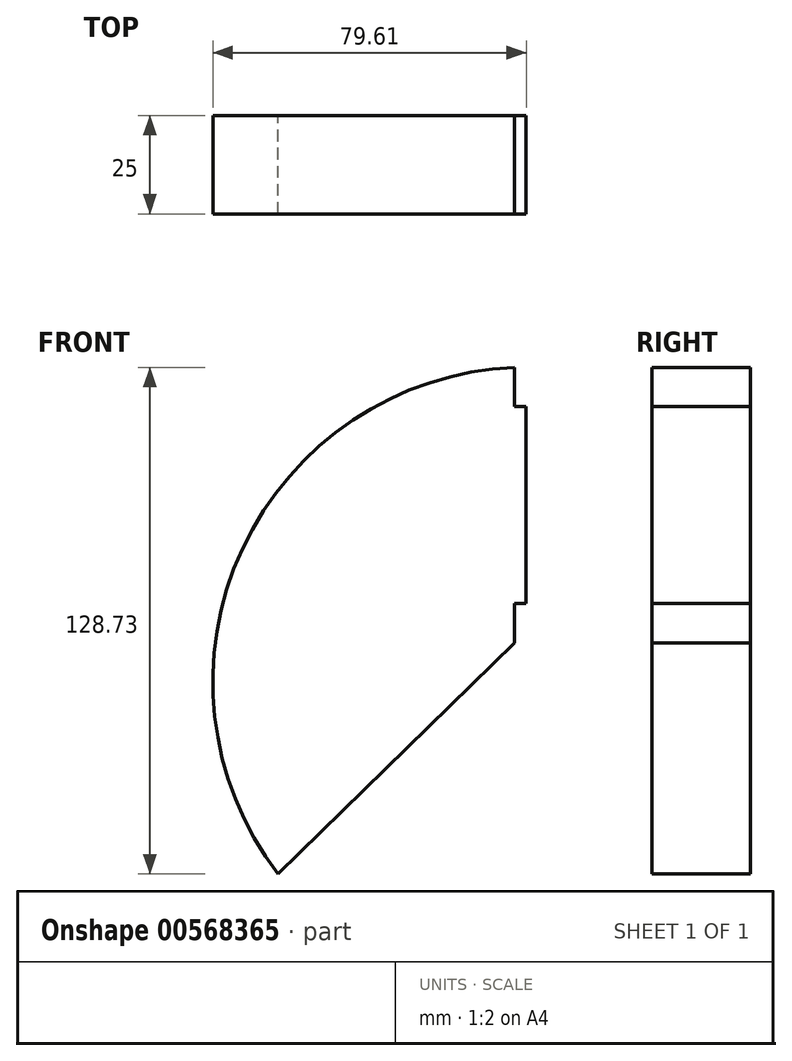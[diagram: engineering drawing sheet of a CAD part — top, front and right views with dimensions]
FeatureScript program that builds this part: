
annotation { "Feature Type Name" : "Feature", "Feature Type Description" : "" }
export const myFeature = defineFeature(function(context is Context, id is Id, definition is map)
    precondition{}
    {
        {
            var Q0;
            Q0=qCreatedBy(makeId("Front.planeOp"),FACE);
            var sketch = newSketch(context, id + "F0", { "sketchPlane" : qUnion([Q0])});
            skArc(sketch, "E0", {"start": v(29.1, 90.46) * mm, "mid": v(-40.01, 44.33) * mm, "end": v(-30.9, -38.27) * mm});
            skLineSegment(sketch, "E1", {"start": v(29.1, 20.46) * mm, "end": v(29.1, 30.46) * mm});
            skLineSegment(sketch, "E2.bottom", {"start": v(29.1, 80.46) * mm, "end": v(32.1, 80.46) * mm});
            skLineSegment(sketch, "E2.top", {"start": v(29.1, 30.46) * mm, "end": v(32.1, 30.46) * mm});
            skLineSegment(sketch, "E2.right", {"start": v(32.1, 80.46) * mm, "end": v(32.1, 30.46) * mm});
            skLineSegment(sketch, "E3.trimOffspring", {"start": v(29.1, 80.46) * mm, "end": v(29.1, 90.46) * mm});
            skLineSegment(sketch, "E4", {"start": v(-30.9, -38.27) * mm, "end": v(29.1, 20.46) * mm});
            skSolve(sketch);
        }
        {
            var Q0;
            Q0=makeQuery(id+"F0.imprint","IMPRINT",FACE,{"disambiguationData":[TD([[makeQuery(id+"F0.imprint","IMPRINT",EDGE,{"derivedFrom":sQuery(id+"F0.wireOp",EDGE,"E0")}),1.0]])]});
            extrude(context, id + "F1", {"entities" : qUnion([Q0]), "depth" : 25 * mm, "offsetDistance" : 25 * mm});
        }
    });
